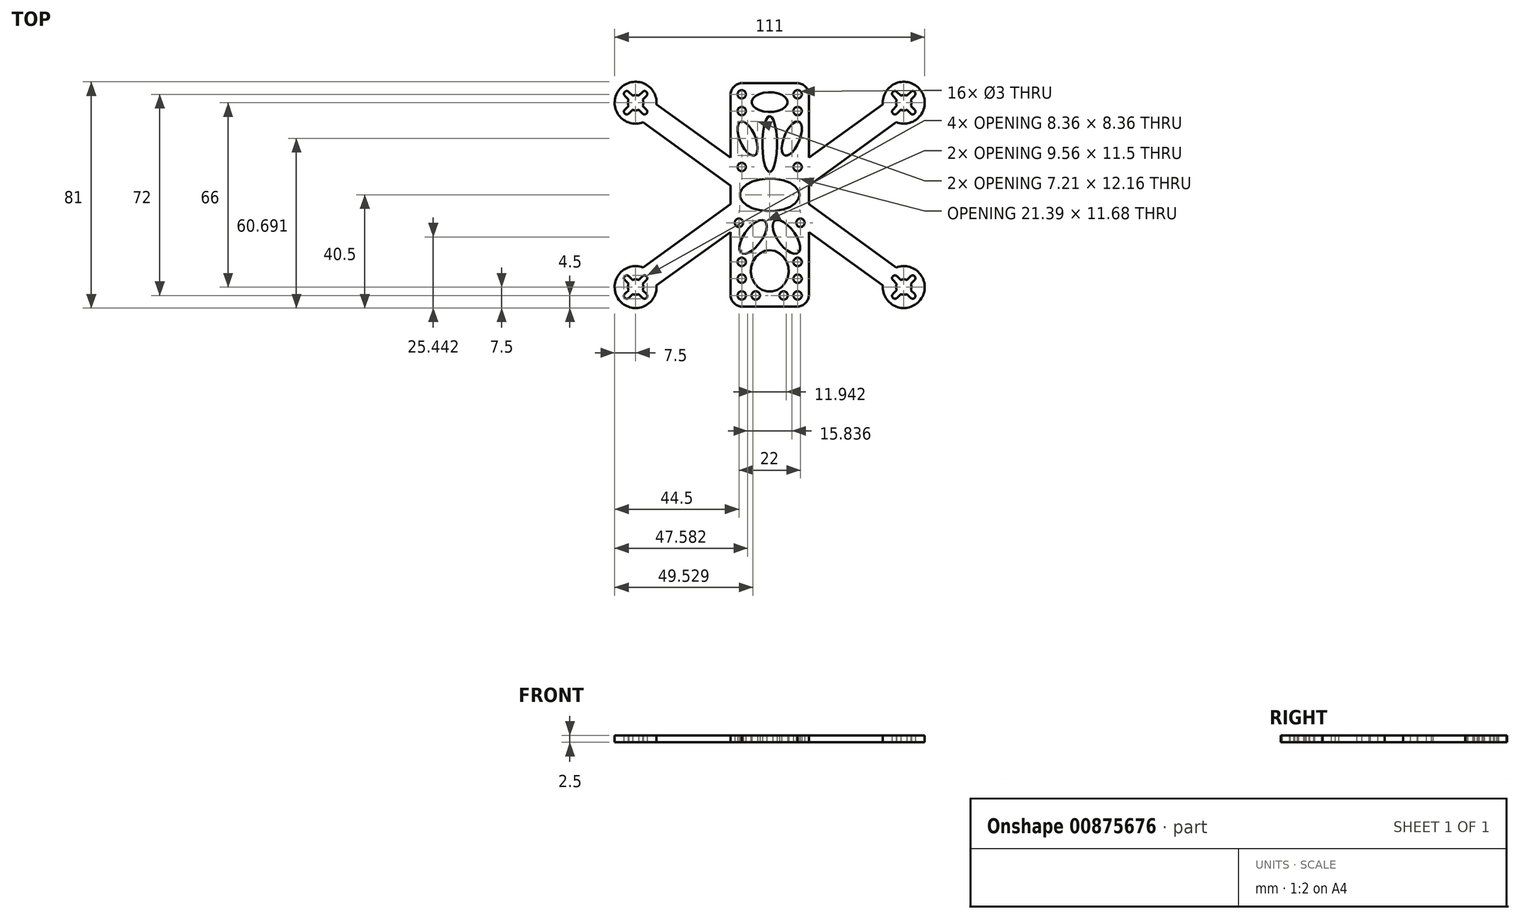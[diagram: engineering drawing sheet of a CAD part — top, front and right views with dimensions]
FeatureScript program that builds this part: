
annotation { "Feature Type Name" : "Feature", "Feature Type Description" : "" }
export const myFeature = defineFeature(function(context is Context, id is Id, definition is map)
    precondition{}
    {
        {
            var Q0;
            Q0=qCreatedBy(makeId("Top.planeOp"),FACE);
            var sketch = newSketch(context, id + "F0", { "sketchPlane" : qUnion([Q0])});
            skPoint(sketch, "E0.middle", {"position": v(0, 0) * mm});
            skCircle(sketch, "E1", {"center": v(48, 33) * mm, "radius": 7.5 * mm});
            skCircle(sketch, "E2.MirrorC", {"center": v(48, -33) * mm, "radius": 7.5 * mm});
            skCircle(sketch, "E3.MirrorC", {"center": v(-48, -33) * mm, "radius": 7.5 * mm});
            skCircle(sketch, "E4.MirrorC", {"center": v(-48, 33) * mm, "radius": 7.5 * mm});
            skCircle(sketch, "E5", {"center": v(-48, 33) * mm, "radius": 2.75 * mm});
            skCircle(sketch, "E6", {"center": v(-44.82, 36.18) * mm, "radius": 1 * mm});
            skLineSegment(sketch, "E7", {"start": v(-45.53, 36.89) * mm, "end": v(-46.9, 35.52) * mm});
            skLineSegment(sketch, "E8", {"start": v(-44.11, 35.47) * mm, "end": v(-45.48, 34.1) * mm});
            skCircle(sketch, "E9.MirrorC", {"center": v(48, 33) * mm, "radius": 2.75 * mm});
            skLineSegment(sketch, "E10.MirrorCS", {"start": v(45.53, 36.89) * mm, "end": v(46.9, 35.52) * mm});
            skCircle(sketch, "E11.MirrorC", {"center": v(44.82, 36.18) * mm, "radius": 1 * mm});
            skLineSegment(sketch, "E12.MirrorCS", {"start": v(44.11, 35.47) * mm, "end": v(45.48, 34.1) * mm});
            skCircle(sketch, "E13.MirrorC", {"center": v(48, -33) * mm, "radius": 2.75 * mm});
            skLineSegment(sketch, "E14.MirrorCS", {"start": v(44.11, -35.47) * mm, "end": v(45.48, -34.1) * mm});
            skCircle(sketch, "E15.MirrorC", {"center": v(44.82, -36.18) * mm, "radius": 1 * mm});
            skLineSegment(sketch, "E16.MirrorCS", {"start": v(45.53, -36.89) * mm, "end": v(46.9, -35.52) * mm});
            skCircle(sketch, "E17.MirrorC", {"center": v(-48, -33) * mm, "radius": 2.75 * mm});
            skLineSegment(sketch, "E18.MirrorCS", {"start": v(-44.11, -35.47) * mm, "end": v(-45.48, -34.1) * mm});
            skCircle(sketch, "E19.MirrorC", {"center": v(-44.82, -36.18) * mm, "radius": 1 * mm});
            skLineSegment(sketch, "E20.MirrorCS", {"start": v(-45.53, -36.89) * mm, "end": v(-46.9, -35.52) * mm});
            skLineSegment(sketch, "E21", {"start": v(14, 13.34) * mm, "end": v(40.53, 32.36) * mm});
            skLineSegment(sketch, "E22", {"start": v(14, 3.3) * mm, "end": v(45.35, 25.98) * mm});
            skCircle(sketch, "E23.MirrorC", {"center": v(51.18, 36.18) * mm, "radius": 1 * mm});
            skCircle(sketch, "E24.MirrorC", {"center": v(51.18, 29.82) * mm, "radius": 1 * mm});
            skCircle(sketch, "E25.MirrorC", {"center": v(44.82, 29.82) * mm, "radius": 1 * mm});
            skLineSegment(sketch, "E26.MirrorCS", {"start": v(-14, 3.3) * mm, "end": v(-45.35, 25.98) * mm});
            skLineSegment(sketch, "E27.MirrorCS", {"start": v(-14, 13.34) * mm, "end": v(-40.53, 32.36) * mm});
            skCircle(sketch, "E28.MirrorC", {"center": v(-44.82, 29.82) * mm, "radius": 1 * mm});
            skCircle(sketch, "E29.MirrorC", {"center": v(-51.18, 29.82) * mm, "radius": 1 * mm});
            skCircle(sketch, "E30.MirrorC", {"center": v(-51.18, 36.18) * mm, "radius": 1 * mm});
            skLineSegment(sketch, "E31.MirrorCS", {"start": v(-14, -13.34) * mm, "end": v(-40.53, -32.36) * mm});
            skLineSegment(sketch, "E32.MirrorCS", {"start": v(-14, -3.3) * mm, "end": v(-45.35, -25.98) * mm});
            skLineSegment(sketch, "E33.MirrorCS", {"start": v(14, -3.3) * mm, "end": v(45.35, -25.98) * mm});
            skLineSegment(sketch, "E34.MirrorCS", {"start": v(14, -13.34) * mm, "end": v(40.53, -32.36) * mm});
            skCircle(sketch, "E35.MirrorC", {"center": v(-44.82, -29.82) * mm, "radius": 1 * mm});
            skCircle(sketch, "E36.MirrorC", {"center": v(-51.18, -29.82) * mm, "radius": 1 * mm});
            skCircle(sketch, "E37.MirrorC", {"center": v(-51.18, -36.18) * mm, "radius": 1 * mm});
            skCircle(sketch, "E38.MirrorC", {"center": v(51.18, -29.82) * mm, "radius": 1 * mm});
            skCircle(sketch, "E39.MirrorC", {"center": v(44.82, -29.82) * mm, "radius": 1 * mm});
            skCircle(sketch, "E40.MirrorC", {"center": v(51.18, -36.18) * mm, "radius": 1 * mm});
            skCircle(sketch, "E41", {"center": v(-10, 36) * mm, "radius": 1.5 * mm});
            skCircle(sketch, "E42.MirrorC", {"center": v(10, 36) * mm, "radius": 1.5 * mm});
            skCircle(sketch, "E43.MirrorC", {"center": v(-10, -36) * mm, "radius": 1.5 * mm});
            skCircle(sketch, "E44.MirrorC", {"center": v(10, -36) * mm, "radius": 1.5 * mm});
            skCircle(sketch, "E45", {"center": v(-10, 10) * mm, "radius": 1.5 * mm});
            skCircle(sketch, "E46.MirrorC", {"center": v(10, 10) * mm, "radius": 1.5 * mm});
            skCircle(sketch, "E47.MirrorC", {"center": v(-10, 30) * mm, "radius": 1.5 * mm});
            skCircle(sketch, "E48.MirrorC", {"center": v(10, 30) * mm, "radius": 1.5 * mm});
            skEllipse(sketch, "E49", {"center": v(0, 18.2) * mm, "majorRadius": 10 * mm, "minorRadius": 2.62 * mm, "majorAxis": v(0, 1)});
            skArc(sketch, "E50", {"start": v(-10, 40) * mm, "mid": v(-12.78, 38.78) * mm, "end": v(-14, 36) * mm});
            skArc(sketch, "E51.MirrorCS", {"start": v(10, 40) * mm, "mid": v(12.78, 38.78) * mm, "end": v(14, 36) * mm});
            skCircle(sketch, "E52.MirrorC", {"center": v(-10, -30) * mm, "radius": 1.5 * mm});
            skCircle(sketch, "E53.MirrorC", {"center": v(10, -30) * mm, "radius": 1.5 * mm});
            skCircle(sketch, "E54.MirrorC", {"center": v(5, -36) * mm, "radius": 1.5 * mm});
            skCircle(sketch, "E55.MirrorC", {"center": v(-5, -36) * mm, "radius": 1.5 * mm});
            skArc(sketch, "E56.MirrorCS", {"start": v(10, -40) * mm, "mid": v(12.78, -38.78) * mm, "end": v(14, -36) * mm});
            skArc(sketch, "E57.MirrorCS", {"start": v(-10, -40) * mm, "mid": v(-12.78, -38.78) * mm, "end": v(-14, -36) * mm});
            skLineSegment(sketch, "E58", {"start": v(-10, 40) * mm, "end": v(10, 40) * mm});
            skLineSegment(sketch, "E59", {"start": v(-14, 36) * mm, "end": v(-14, -36) * mm});
            skLineSegment(sketch, "E60", {"start": v(14, -36) * mm, "end": v(14, 36) * mm});
            skLineSegment(sketch, "E61", {"start": v(-10, -40) * mm, "end": v(10, -40) * mm});
            skCircle(sketch, "E62.MirrorC", {"center": v(-10, -24) * mm, "radius": 1.5 * mm});
            skCircle(sketch, "E63.MirrorC", {"center": v(10, -24) * mm, "radius": 1.5 * mm});
            skCircle(sketch, "E64", {"center": v(-11, -10) * mm, "radius": 1.5 * mm});
            skCircle(sketch, "E65.MirrorC", {"center": v(11, -10) * mm, "radius": 1.5 * mm});
            skPoint(sketch, "E66.middle", {"position": v(0, -16.36) * mm});
            skPoint(sketch, "E67", {"position": v(0, -6.6) * mm});
            skPoint(sketch, "E68", {"position": v(0, -35.25) * mm});
            skPoint(sketch, "E69", {"position": v(0, 22.36) * mm});
            skPoint(sketch, "E69.positionSnap0", {"position": v(0, 28.2) * mm});
            skLineSegment(sketch, "E70.MirrorCS", {"start": v(44.11, 30.53) * mm, "end": v(45.48, 31.9) * mm});
            skLineSegment(sketch, "E71.MirrorCS", {"start": v(44.11, -30.53) * mm, "end": v(45.48, -31.9) * mm});
            skLineSegment(sketch, "E72.MirrorCS", {"start": v(-44.11, -30.53) * mm, "end": v(-45.48, -31.9) * mm});
            skLineSegment(sketch, "E73.MirrorCS", {"start": v(45.53, 29.11) * mm, "end": v(46.9, 30.48) * mm});
            skLineSegment(sketch, "E74.MirrorCS", {"start": v(50.47, 29.11) * mm, "end": v(49.1, 30.48) * mm});
            skLineSegment(sketch, "E75.MirrorCS", {"start": v(51.89, 30.53) * mm, "end": v(50.52, 31.9) * mm});
            skLineSegment(sketch, "E76.MirrorCS", {"start": v(51.89, 35.47) * mm, "end": v(50.52, 34.1) * mm});
            skLineSegment(sketch, "E77.MirrorCS", {"start": v(50.47, 36.89) * mm, "end": v(49.1, 35.52) * mm});
            skLineSegment(sketch, "E78.MirrorCS", {"start": v(-45.53, 29.11) * mm, "end": v(-46.9, 30.48) * mm});
            skLineSegment(sketch, "E79.MirrorCS", {"start": v(-50.47, 29.11) * mm, "end": v(-49.1, 30.48) * mm});
            skLineSegment(sketch, "E80.MirrorCS", {"start": v(-51.89, 30.53) * mm, "end": v(-50.52, 31.9) * mm});
            skLineSegment(sketch, "E81.MirrorCS", {"start": v(-51.89, 35.47) * mm, "end": v(-50.52, 34.1) * mm});
            skLineSegment(sketch, "E82.MirrorCS", {"start": v(-50.47, 36.89) * mm, "end": v(-49.1, 35.52) * mm});
            skLineSegment(sketch, "E83.MirrorCS", {"start": v(50.47, -36.89) * mm, "end": v(49.1, -35.52) * mm});
            skLineSegment(sketch, "E84.MirrorCS", {"start": v(51.89, -35.47) * mm, "end": v(50.52, -34.1) * mm});
            skLineSegment(sketch, "E85.MirrorCS", {"start": v(51.89, -30.53) * mm, "end": v(50.52, -31.9) * mm});
            skLineSegment(sketch, "E86.MirrorCS", {"start": v(50.47, -29.11) * mm, "end": v(49.1, -30.48) * mm});
            skLineSegment(sketch, "E87.MirrorCS", {"start": v(45.53, -29.11) * mm, "end": v(46.9, -30.48) * mm});
            skLineSegment(sketch, "E88.MirrorCS", {"start": v(-45.53, -29.11) * mm, "end": v(-46.9, -30.48) * mm});
            skLineSegment(sketch, "E89.MirrorCS", {"start": v(-50.47, -29.11) * mm, "end": v(-49.1, -30.48) * mm});
            skLineSegment(sketch, "E90.MirrorCS", {"start": v(-51.89, -30.53) * mm, "end": v(-50.52, -31.9) * mm});
            skLineSegment(sketch, "E91.MirrorCS", {"start": v(-51.89, -35.47) * mm, "end": v(-50.52, -34.1) * mm});
            skLineSegment(sketch, "E92.MirrorCS", {"start": v(-50.47, -36.89) * mm, "end": v(-49.1, -35.52) * mm});
            skLineSegment(sketch, "E93.MirrorCS", {"start": v(-44.11, 30.53) * mm, "end": v(-45.48, 31.9) * mm});
            skPoint(sketch, "E94.middle", {"position": v(0, -3.7) * mm});
            skEllipse(sketch, "E95", {"center": v(-7.92, 20.2) * mm, "majorRadius": 6.58 * mm, "minorRadius": 2.78 * mm, "majorAxis": v(0.38, -0.92)});
            skEllipse(sketch, "E96.MirrorC", {"center": v(7.92, 20.2) * mm, "majorRadius": 6.58 * mm, "minorRadius": 2.78 * mm, "majorAxis": v(-0.38, -0.92)});
            skEllipse(sketch, "E97", {"center": v(0, 0) * mm, "majorRadius": 10.7 * mm, "minorRadius": 5.84 * mm, "majorAxis": v(1, 0)});
            skEllipse(sketch, "E98", {"center": v(-5.97, -15.06) * mm, "majorRadius": 7.1 * mm, "minorRadius": 3.2 * mm, "majorAxis": v(0.59, 0.8)});
            skEllipse(sketch, "E99.MirrorC", {"center": v(5.97, -15.06) * mm, "majorRadius": 7.1 * mm, "minorRadius": 3.2 * mm, "majorAxis": v(-0.59, 0.8)});
            skEllipse(sketch, "E100", {"center": v(0, -27.24) * mm, "majorRadius": 6.79 * mm, "minorRadius": 7.41 * mm, "majorAxis": v(1, 0)});
            skEllipse(sketch, "E101", {"center": v(0, 33.22) * mm, "majorRadius": 6.4 * mm, "minorRadius": 3.53 * mm, "majorAxis": v(1, 0)});
            skSolve(sketch);
        }
        {
            var Q0;
            Q0=qSketchRegion(id+"F0",true);
            extrude(context, id + "F1", {"entities" : qUnion([Q0]), "depth" : 2.5 * mm, "offsetDistance" : 25 * mm});
        }
    });
